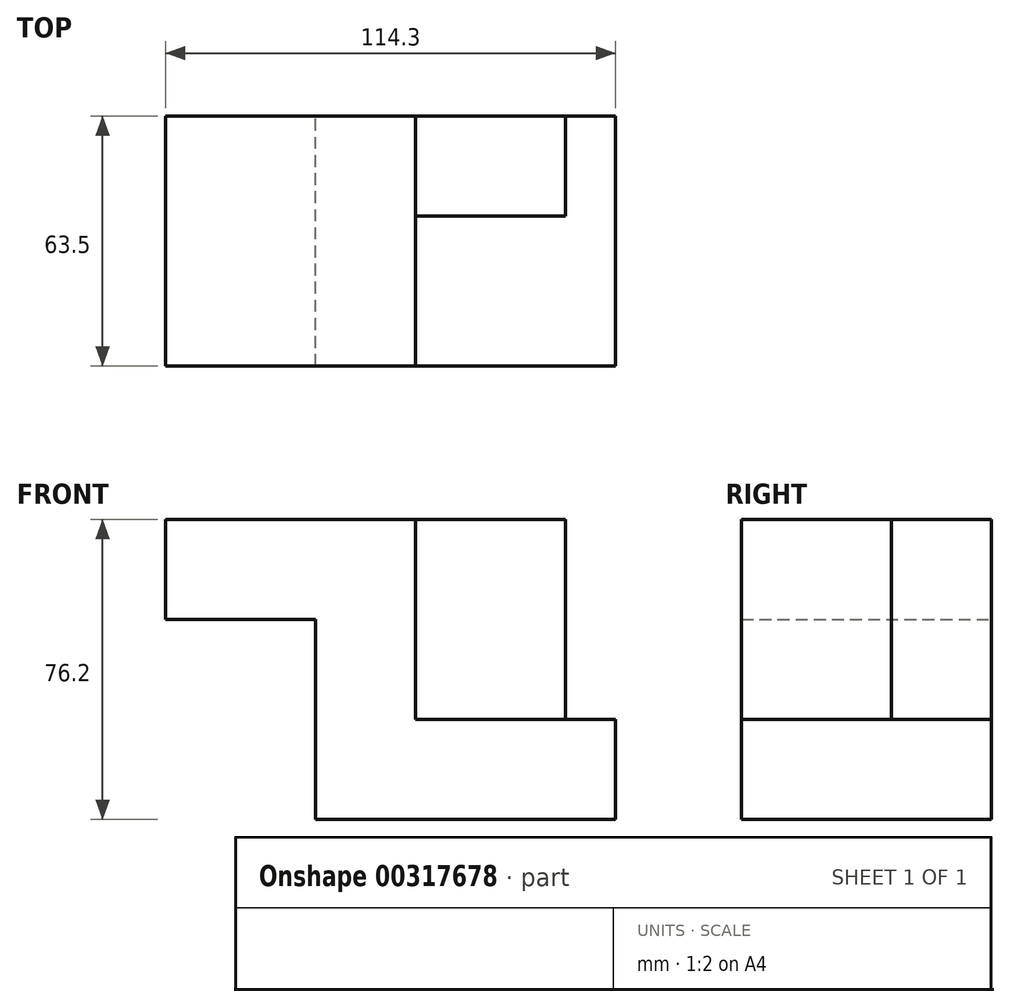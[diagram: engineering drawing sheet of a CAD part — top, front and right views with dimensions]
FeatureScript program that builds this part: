
annotation { "Feature Type Name" : "Feature", "Feature Type Description" : "" }
export const myFeature = defineFeature(function(context is Context, id is Id, definition is map)
    precondition{}
    {
        {
            var Q0;
            Q0=qCreatedBy(makeId("Front.planeOp"),FACE);
            var sketch = newSketch(context, id + "F0", { "sketchPlane" : qUnion([Q0])});
            skLineSegment(sketch, "E0", {"start": v(-60.47, 50.8) * mm, "end": v(-60.47, 25.4) * mm});
            skLineSegment(sketch, "E1", {"start": v(-60.47, 50.8) * mm, "end": v(3.03, 50.8) * mm});
            skLineSegment(sketch, "E2", {"start": v(-60.47, 25.4) * mm, "end": v(-22.37, 25.4) * mm});
            skLineSegment(sketch, "E3", {"start": v(3.03, 50.8) * mm, "end": v(3.03, 0) * mm});
            skLineSegment(sketch, "E4", {"start": v(-22.37, 25.4) * mm, "end": v(-22.37, -25.4) * mm});
            skLineSegment(sketch, "E5", {"start": v(-22.37, -25.4) * mm, "end": v(53.83, -25.4) * mm});
            skLineSegment(sketch, "E6", {"start": v(53.83, -25.4) * mm, "end": v(53.83, 0) * mm});
            skLineSegment(sketch, "E7", {"start": v(53.83, 0) * mm, "end": v(3.03, 0) * mm});
            skSolve(sketch);
        }
        {
            var Q0;
            Q0 = qSketchRegion(id + "F0", true);
            extrude(context, id + "F1", {"entities" : qUnion([Q0]), "depth" : 63.5 * mm});
        }
        {
            var Q0;
            Q0=makeQuery(id+"F1.opExtrude","CAP_FACE",FACE,{"disambiguationData":[OSD([sQuery(id+"F0.wireOp",EDGE,"E0"),sQuery(id+"F0.wireOp",EDGE,"E1"),sQuery(id+"F0.wireOp",EDGE,"E2"),sQuery(id+"F0.wireOp",EDGE,"E3"),sQuery(id+"F0.wireOp",EDGE,"E4"),sQuery(id+"F0.wireOp",EDGE,"E5"),sQuery(id+"F0.wireOp",EDGE,"E6"),sQuery(id+"F0.wireOp",EDGE,"E7")])],"isStart":true});
            var sketch = newSketch(context, id + "F2", { "sketchPlane" : qUnion([Q0])});
            skLineSegment(sketch, "E8", {"start": v(-3.03, 50.8) * mm, "end": v(-3.03, 0) * mm});
            skLineSegment(sketch, "E9", {"start": v(-3.03, 0) * mm, "end": v(-41.13, 0) * mm});
            skLineSegment(sketch, "E10", {"start": v(-41.13, 0) * mm, "end": v(-41.13, 50.8) * mm});
            skLineSegment(sketch, "E11", {"start": v(-41.13, 50.8) * mm, "end": v(-3.03, 50.8) * mm});
            skSolve(sketch);
        }
        {
            var Q0;
            Q0 = qSketchRegion(id + "F2", true);
            extrude(context, id + "F3", {"entities" : qUnion([Q0]), "oppositeDirection" : true, "depth" : 25.4 * mm});
        }
    });
